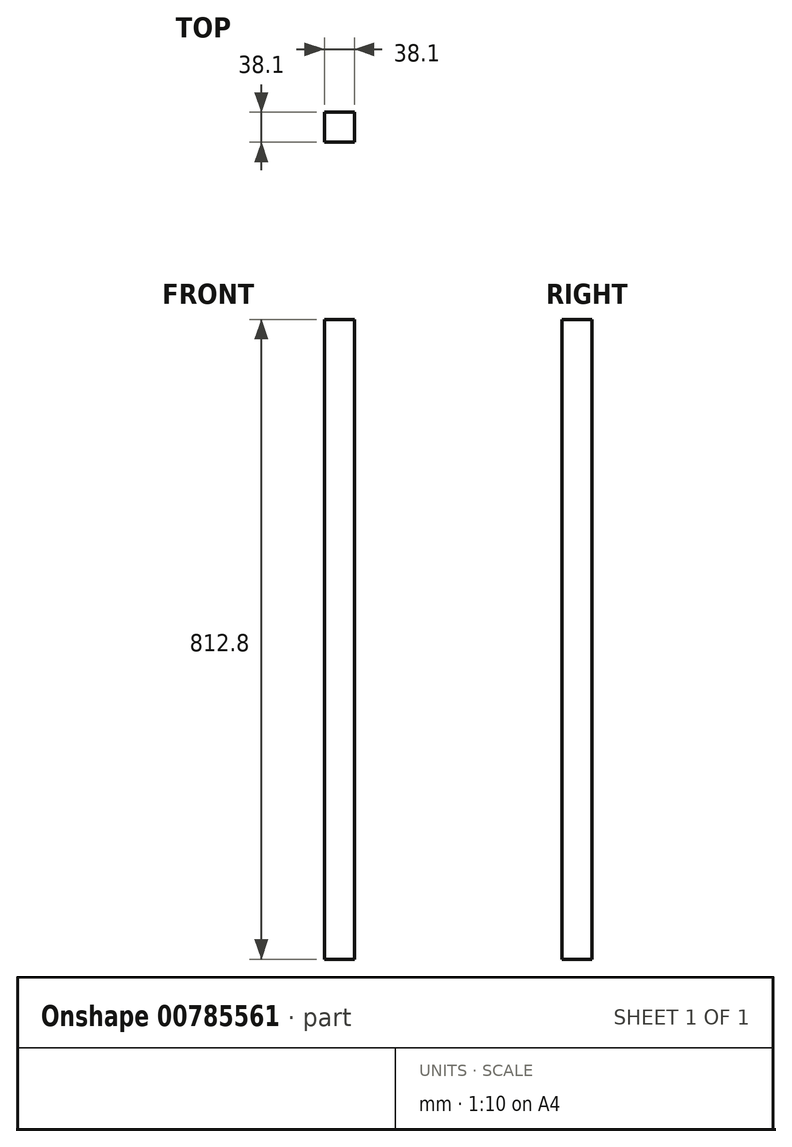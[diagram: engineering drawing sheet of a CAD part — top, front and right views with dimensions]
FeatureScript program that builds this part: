
annotation { "Feature Type Name" : "Feature", "Feature Type Description" : "" }
export const myFeature = defineFeature(function(context is Context, id is Id, definition is map)
    precondition{}
    {
        {
            var Q0;
            Q0=qCreatedBy(makeId("Top.planeOp"),FACE);
            var sketch = newSketch(context, id + "F0", { "sketchPlane" : qUnion([Q0])});
            skLineSegment(sketch, "E0.bottom", {"start": v(19.05, 19.05) * mm, "end": v(-19.05, 19.05) * mm});
            skLineSegment(sketch, "E0.top", {"start": v(19.05, -19.05) * mm, "end": v(-19.05, -19.05) * mm});
            skLineSegment(sketch, "E0.left", {"start": v(19.05, 19.05) * mm, "end": v(19.05, -19.05) * mm});
            skLineSegment(sketch, "E0.right", {"start": v(-19.05, 19.05) * mm, "end": v(-19.05, -19.05) * mm});
            skPoint(sketch, "E0.middle", {"position": v(0, 0) * mm});
            skSolve(sketch);
        }
        {
            var Q0;
            Q0 = qSketchRegion(id + "F0", true);
            extrude(context, id + "F1", {"entities" : qUnion([Q0]), "depth" : 812.8 * mm, "offsetDistance" : 25.4 * mm});
        }
    });
